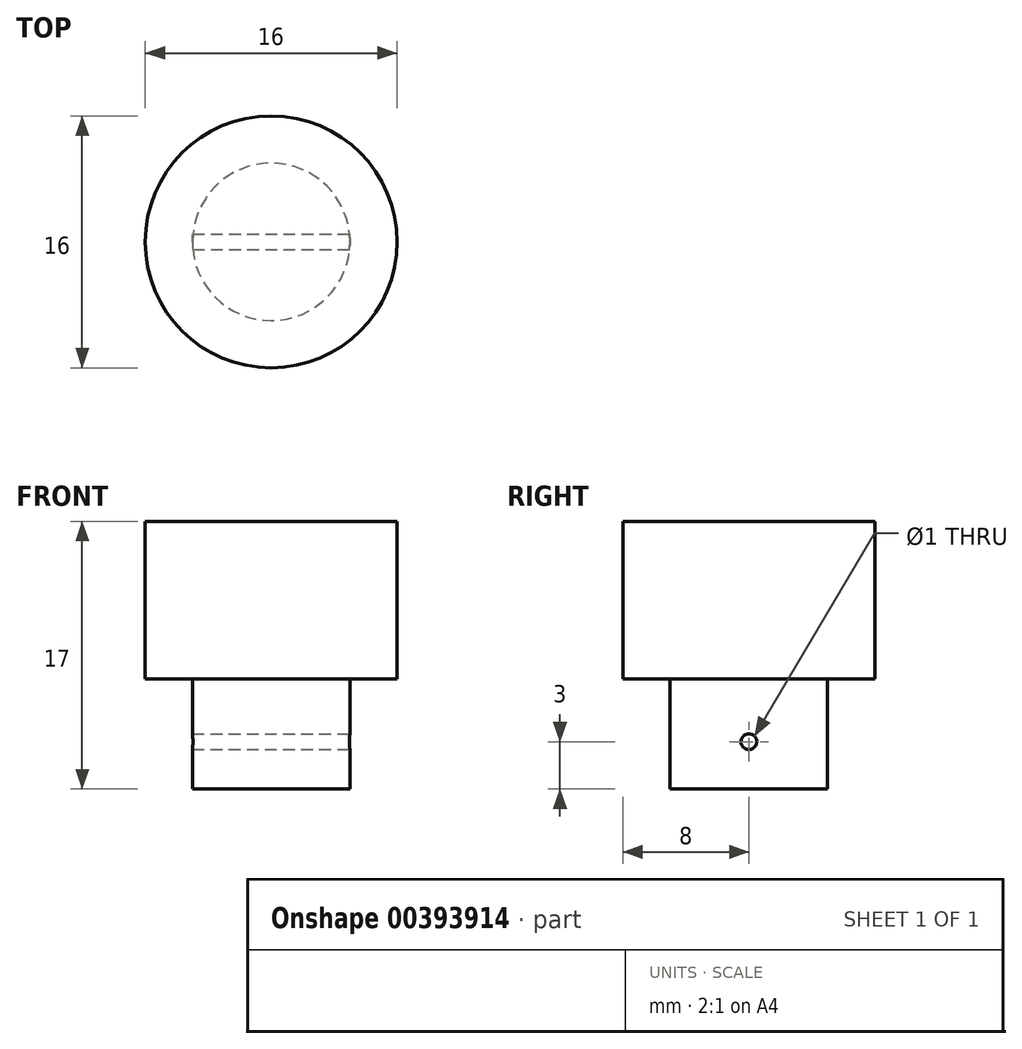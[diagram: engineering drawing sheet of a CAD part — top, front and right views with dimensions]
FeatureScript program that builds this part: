
annotation { "Feature Type Name" : "Feature", "Feature Type Description" : "" }
export const myFeature = defineFeature(function(context is Context, id is Id, definition is map)
    precondition{}
    {
        {
            var Q0;
            Q0=qCreatedBy(makeId("Top.planeOp"),FACE);
            var sketch = newSketch(context, id + "F0", { "sketchPlane" : qUnion([Q0])});
            skCircle(sketch, "E0", {"center": v(0, 0) * mm, "radius": 8 * mm});
            skSolve(sketch);
        }
        {
            var Q0;
            Q0=makeQuery(id+"F0.imprint","IMPRINT",FACE,{"disambiguationData":[TD([[makeQuery(id+"F0.imprint","IMPRINT",EDGE,{"derivedFrom":sQuery(id+"F0.wireOp",EDGE,"E0")}),1.0]])]});
            extrude(context, id + "F1", {"entities" : qUnion([Q0]), "depth" : 10 * mm});
        }
        {
            var Q0;
            Q0=makeQuery(id+"F1.opExtrude","CAP_FACE",FACE,{"disambiguationData":[OSD([sQuery(id+"F0.wireOp",EDGE,"E0")])],"isStart":true});
            var sketch = newSketch(context, id + "F2", { "sketchPlane" : qUnion([Q0])});
            skCircle(sketch, "E1", {"center": v(0, 0) * mm, "radius": 5 * mm});
            skSolve(sketch);
        }
        {
            var Q0;
            Q0=makeQuery(id+"F2.imprint","IMPRINT",FACE,{"disambiguationData":[TD([[makeQuery(id+"F2.imprint","IMPRINT",EDGE,{"derivedFrom":sQuery(id+"F2.wireOp",EDGE,"E1")}),1.0]])]});
            extrude(context, id + "F3", {"entities" : qUnion([Q0]), "operationType" : NewBodyOperationType.ADD, "depth" : 7 * mm});
        }
        {
            var Q0;
            Q0=qCreatedBy(makeId("Right.planeOp"),FACE);
            var sketch = newSketch(context, id + "F4", { "sketchPlane" : qUnion([Q0])});
            skCircle(sketch, "E2", {"center": v(0, -4) * mm, "radius": 0.5 * mm});
            skSolve(sketch);
        }
        {
            var Q0;
            Q0 = qSketchRegion(id + "F4", true);
            extrude(context, id + "F5", {"entities" : qUnion([Q0]), "operationType" : NewBodyOperationType.REMOVE, "oppositeDirection" : true, "depth" : 25 * mm});
        }
        {
            var Q0;
            Q0=makeQuery(id+"F5.boolean.opBoolean","COPY",FACE,{"derivedFrom":makeQuery(id+"F5.opExtrude","CAP_FACE",FACE,{"disambiguationData":[OSD([sQuery(id+"F4.wireOp",EDGE,"E2")])],"isStart":true})});
            var sketch = newSketch(context, id + "F6", { "sketchPlane" : qUnion([Q0])});
            skCircle(sketch, "E3", {"center": v(0, -4) * mm, "radius": 0.5 * mm});
            skSolve(sketch);
        }
        {
            var Q0;
            Q0=makeQuery(id+"F6.imprint","IMPRINT",FACE,{"disambiguationData":[TD([[makeQuery(id+"F6.imprint","IMPRINT",EDGE,{"derivedFrom":sQuery(id+"F6.wireOp",EDGE,"E3")}),-1.0]])]});
            extrude(context, id + "F7", {"entities" : qUnion([Q0]), "operationType" : NewBodyOperationType.REMOVE, "oppositeDirection" : true, "depth" : 25 * mm});
        }
    });
